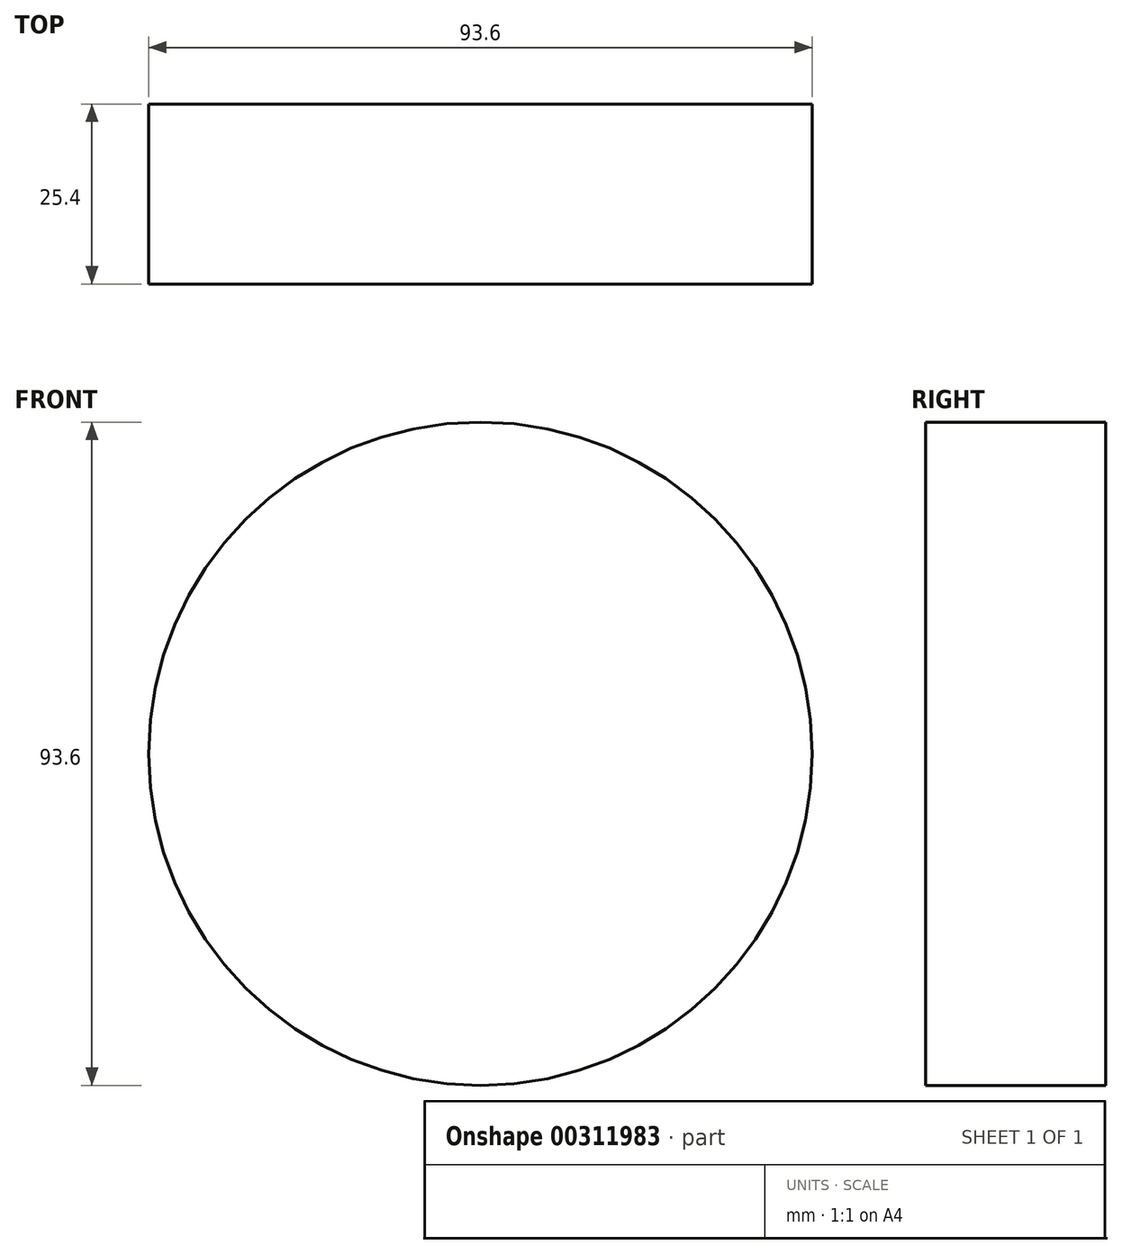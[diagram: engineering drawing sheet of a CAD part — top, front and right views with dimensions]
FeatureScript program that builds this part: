
annotation { "Feature Type Name" : "Feature", "Feature Type Description" : "" }
export const myFeature = defineFeature(function(context is Context, id is Id, definition is map)
    precondition{}
    {
        {
            var Q0;
            Q0=qCreatedBy(makeId("Front.planeOp"),FACE);
            var sketch = newSketch(context, id + "F0", { "sketchPlane" : qUnion([Q0])});
            skCircle(sketch, "E0", {"center": v(0, 0) * mm, "radius": 46.8 * mm});
            skSolve(sketch);
        }
        {
            var Q0;
            Q0=makeQuery(id+"F0.imprint","IMPRINT",FACE,{"disambiguationData":[TD([[makeQuery(id+"F0.imprint","IMPRINT",EDGE,{"derivedFrom":sQuery(id+"F0.wireOp",EDGE,"E0")}),1.0]])]});
            extrude(context, id + "F1", {"entities" : qUnion([Q0]), "depth" : 25.4 * mm});
        }
        {
            var Q0;
            Q0=makeQuery(id+"F1.opExtrude","CAP_FACE",FACE,{"disambiguationData":[OSD([sQuery(id+"F0.wireOp",EDGE,"E0")])],"isStart":true});
            var sketch = newSketch(context, id + "F2", { "sketchPlane" : qUnion([Q0])});
            skCircle(sketch, "E1", {"center": v(17.68, 19.55) * mm, "radius": 8.05 * mm});
            skCircle(sketch, "E2", {"center": v(20.11, -17.3) * mm, "radius": 7.13 * mm});
            skCircle(sketch, "E3", {"center": v(-21.26, -17.58) * mm, "radius": 6.01 * mm});
            skCircle(sketch, "E4", {"center": v(-17.68, 24.08) * mm, "radius": 5.45 * mm});
            skSolve(sketch);
        }
        {
            var Q0;
            Q0=sQuery(id+"F2.wireOp",EDGE,"E2");
            var Q1;
            Q1=sQuery(id+"F2.wireOp",EDGE,"E3");
            var Q2;
            Q2=sQuery(id+"F2.wireOp",EDGE,"E1");
            var Q3;
            Q3=sQuery(id+"F2.wireOp",EDGE,"E4");
            extrude(context, id + "F3", {"bodyType" : ToolBodyType.SURFACE, "surfaceEntities" : qUnion([Q0, Q1, Q2, Q3]), "depth" : 304.8 * mm});
        }
    });
